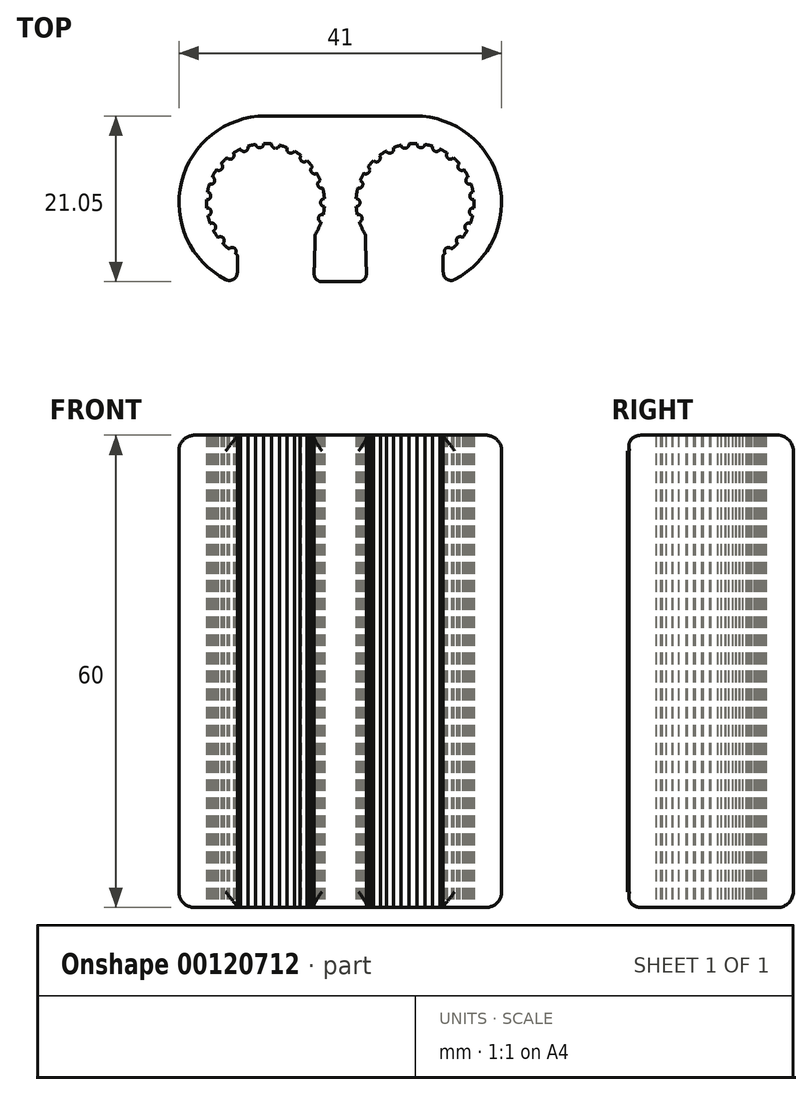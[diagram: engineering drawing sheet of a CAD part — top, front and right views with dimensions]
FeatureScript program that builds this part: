
annotation { "Feature Type Name" : "Feature", "Feature Type Description" : "" }
export const myFeature = defineFeature(function(context is Context, id is Id, definition is map)
    precondition{}
    {
        {
            var Q0;
            Q0=qCreatedBy(makeId("Top.planeOp"),FACE);
            var sketch = newSketch(context, id + "F0", { "sketchPlane" : qUnion([Q0])});
            skArc(sketch, "E0", {"start": v(13.27, -6.48) * mm, "mid": v(11.32, 7.28) * mm, "end": v(3.12, -3.94) * mm});
            skArc(sketch, "E1", {"start": v(-3.12, -3.94) * mm, "mid": v(-11.32, 7.28) * mm, "end": v(-13.27, -6.48) * mm});
            skArc(sketch, "E2", {"start": v(14.54, -9.78) * mm, "mid": v(20.2, 2.6) * mm, "end": v(9.5, 11) * mm});
            skArc(sketch, "E3", {"start": v(-9.5, 11) * mm, "mid": v(-20.2, 2.6) * mm, "end": v(-14.54, -9.78) * mm});
            skLineSegment(sketch, "E4.left", {"start": v(13.08, -8.92) * mm, "end": v(13.03, -6.93) * mm});
            skLineSegment(sketch, "E4.right", {"start": v(3.33, -9.02) * mm, "end": v(3.19, -4.18) * mm});
            skLineSegment(sketch, "E5.bottom", {"start": v(2.33, -10.05) * mm, "end": v(-2.33, -10.05) * mm});
            skLineSegment(sketch, "E5.top", {"start": v(9.5, 11) * mm, "end": v(-9.5, 11) * mm});
            skLineSegment(sketch, "E6.MirrorCS", {"start": v(-3.33, -9.02) * mm, "end": v(-3.19, -4.18) * mm});
            skLineSegment(sketch, "E7.MirrorCS", {"start": v(-13.08, -8.92) * mm, "end": v(-13.03, -6.93) * mm});
            skArc(sketch, "E8.filletArc", {"start": v(-14.54, -9.78) * mm, "mid": v(-13.57, -9.75) * mm, "end": v(-13.08, -8.92) * mm});
            skArc(sketch, "E9.filletArc", {"start": v(-3.33, -9.02) * mm, "mid": v(-3.04, -9.74) * mm, "end": v(-2.33, -10.05) * mm});
            skArc(sketch, "E10.filletArc", {"start": v(2.33, -10.05) * mm, "mid": v(3.04, -9.74) * mm, "end": v(3.33, -9.02) * mm});
            skArc(sketch, "E11.filletArc", {"start": v(13.08, -8.92) * mm, "mid": v(13.57, -9.75) * mm, "end": v(14.54, -9.78) * mm});
            skArc(sketch, "E12.filletArc", {"start": v(-13.03, -6.93) * mm, "mid": v(-13.09, -6.67) * mm, "end": v(-13.27, -6.48) * mm});
            skArc(sketch, "E13.filletArc", {"start": v(-3.12, -3.94) * mm, "mid": v(-3.17, -4.05) * mm, "end": v(-3.19, -4.18) * mm});
            skArc(sketch, "E14.filletArc", {"start": v(3.19, -4.18) * mm, "mid": v(3.17, -4.05) * mm, "end": v(3.12, -3.94) * mm});
            skArc(sketch, "E15.filletArc", {"start": v(13.27, -6.48) * mm, "mid": v(13.09, -6.67) * mm, "end": v(13.03, -6.93) * mm});
            skCircle(sketch, "E16", {"center": v(-2, 0) * mm, "radius": 0.5 * mm});
            skCircle(sketch, "E17.1.0", {"center": v(-2.27, -2.01) * mm, "radius": 0.5 * mm});
            skCircle(sketch, "E17.8.0", {"center": v(-13.73, -6.2) * mm, "radius": 0.5 * mm});
            skCircle(sketch, "E17.9.0", {"center": v(-15.24, -4.83) * mm, "radius": 0.5 * mm});
            skCircle(sketch, "E17.10.0", {"center": v(-16.32, -3.12) * mm, "radius": 0.5 * mm});
            skCircle(sketch, "E17.11.0", {"center": v(-16.9, -1.17) * mm, "radius": 0.5 * mm});
            skCircle(sketch, "E17.12.0", {"center": v(-16.95, 0.85) * mm, "radius": 0.5 * mm});
            skCircle(sketch, "E17.13.0", {"center": v(-16.45, 2.82) * mm, "radius": 0.5 * mm});
            skCircle(sketch, "E17.14.0", {"center": v(-15.44, 4.58) * mm, "radius": 0.5 * mm});
            skLineSegment(sketch, "E17.anchor1", {"start": v(-9.5, 0) * mm, "end": v(-2, 0) * mm, "construction": true});
            skLineSegment(sketch, "E17.anchor2", {"start": v(-9.5, 0) * mm, "end": v(-2.37, 2.32) * mm, "construction": true});
            skCircle(sketch, "E18.1.15.0", {"center": v(-14, 6) * mm, "radius": 0.5 * mm});
            skCircle(sketch, "E18.1.16.0", {"center": v(-12.22, 6.99) * mm, "radius": 0.5 * mm});
            skCircle(sketch, "E18.1.17.0", {"center": v(-10.25, 7.46) * mm, "radius": 0.5 * mm});
            skCircle(sketch, "E18.1.18.0", {"center": v(-8.22, 7.4) * mm, "radius": 0.5 * mm});
            skCircle(sketch, "E18.1.19.0", {"center": v(-6.29, 6.78) * mm, "radius": 0.5 * mm});
            skCircle(sketch, "E18.1.20.0", {"center": v(-4.59, 5.67) * mm, "radius": 0.5 * mm});
            skCircle(sketch, "E19.1.21.0", {"center": v(-3.25, 4.14) * mm, "radius": 0.5 * mm});
            skCircle(sketch, "E20.1.22.0", {"center": v(-2.37, 2.32) * mm, "radius": 0.5 * mm});
            skCircle(sketch, "E21.MirrorC", {"center": v(2, 0) * mm, "radius": 0.5 * mm});
            skCircle(sketch, "E22.MirrorC", {"center": v(2.37, 2.32) * mm, "radius": 0.5 * mm});
            skCircle(sketch, "E23.MirrorC", {"center": v(3.25, 4.14) * mm, "radius": 0.5 * mm});
            skCircle(sketch, "E24.MirrorC", {"center": v(4.59, 5.67) * mm, "radius": 0.5 * mm});
            skCircle(sketch, "E25.MirrorC", {"center": v(6.29, 6.78) * mm, "radius": 0.5 * mm});
            skCircle(sketch, "E26.MirrorC", {"center": v(8.22, 7.4) * mm, "radius": 0.5 * mm});
            skCircle(sketch, "E27.MirrorC", {"center": v(10.25, 7.46) * mm, "radius": 0.5 * mm});
            skCircle(sketch, "E28.MirrorC", {"center": v(12.22, 6.99) * mm, "radius": 0.5 * mm});
            skCircle(sketch, "E29.MirrorC", {"center": v(14, 6) * mm, "radius": 0.5 * mm});
            skCircle(sketch, "E30.MirrorC", {"center": v(15.44, 4.58) * mm, "radius": 0.5 * mm});
            skCircle(sketch, "E31.MirrorC", {"center": v(16.45, 2.82) * mm, "radius": 0.5 * mm});
            skCircle(sketch, "E32.MirrorC", {"center": v(16.95, 0.85) * mm, "radius": 0.5 * mm});
            skCircle(sketch, "E33.MirrorC", {"center": v(16.9, -1.17) * mm, "radius": 0.5 * mm});
            skCircle(sketch, "E34.MirrorC", {"center": v(16.32, -3.12) * mm, "radius": 0.5 * mm});
            skCircle(sketch, "E35.MirrorC", {"center": v(15.24, -4.83) * mm, "radius": 0.5 * mm});
            skCircle(sketch, "E36.MirrorC", {"center": v(13.73, -6.2) * mm, "radius": 0.5 * mm});
            skCircle(sketch, "E37.MirrorC", {"center": v(2.27, -2.01) * mm, "radius": 0.5 * mm});
            skSolve(sketch);
        }
        {
            var Q0;
            Q0 = qSketchRegion(id + "F0", true);
            extrude(context, id + "F1", {"entities" : qUnion([Q0]), "endBound" : BoundingType.SYMMETRIC, "depth" : 60 * mm});
        }
        {
            var Q0;
            Q0=makeQuery(id+"F1.opExtrude","CAP_EDGE",EDGE,{"disambiguationData":[OSD([sQuery(id+"F0.wireOp",EDGE,"E5.top")])],"isStart":false});
            var Q1;
            Q1=makeQuery(id+"F1.opExtrude","CAP_EDGE",EDGE,{"disambiguationData":[OSD([sQuery(id+"F0.wireOp",EDGE,"E3")])],"isStart":false});
            var Q2;
            Q2=makeQuery(id+"F1.opExtrude","CAP_EDGE",EDGE,{"disambiguationData":[OSD([sQuery(id+"F0.wireOp",EDGE,"E2")])],"isStart":false});
            var Q3;
            Q3=makeQuery(id+"F1.opExtrude","CAP_EDGE",EDGE,{"disambiguationData":[OSD([sQuery(id+"F0.wireOp",EDGE,"E5.bottom")])],"isStart":false});
            fillet(context, id + "F2", {"entities" : qUnion([Q0, Q1, Q2, Q3]), "radius" : 2 * mm, "allowEdgeOverflow" : false});
        }
        {
            var Q0;
            Q0=makeQuery(id+"F1.opExtrude","CAP_EDGE",EDGE,{"disambiguationData":[OSD([sQuery(id+"F0.wireOp",EDGE,"E3")])],"isStart":true});
            var Q1;
            Q1=makeQuery(id+"F1.opExtrude","CAP_EDGE",EDGE,{"disambiguationData":[OSD([sQuery(id+"F0.wireOp",EDGE,"E5.bottom")])],"isStart":true});
            var Q2;
            Q2=makeQuery(id+"F1.opExtrude","CAP_EDGE",EDGE,{"disambiguationData":[OSD([sQuery(id+"F0.wireOp",EDGE,"E2")])],"isStart":true});
            var Q3;
            Q3=makeQuery(id+"F1.opExtrude","CAP_EDGE",EDGE,{"disambiguationData":[OSD([sQuery(id+"F0.wireOp",EDGE,"E5.top")])],"isStart":true});
            fillet(context, id + "F3", {"entities" : qUnion([Q0, Q1, Q2, Q3]), "radius" : 2 * mm, "allowEdgeOverflow" : false});
        }
    });
